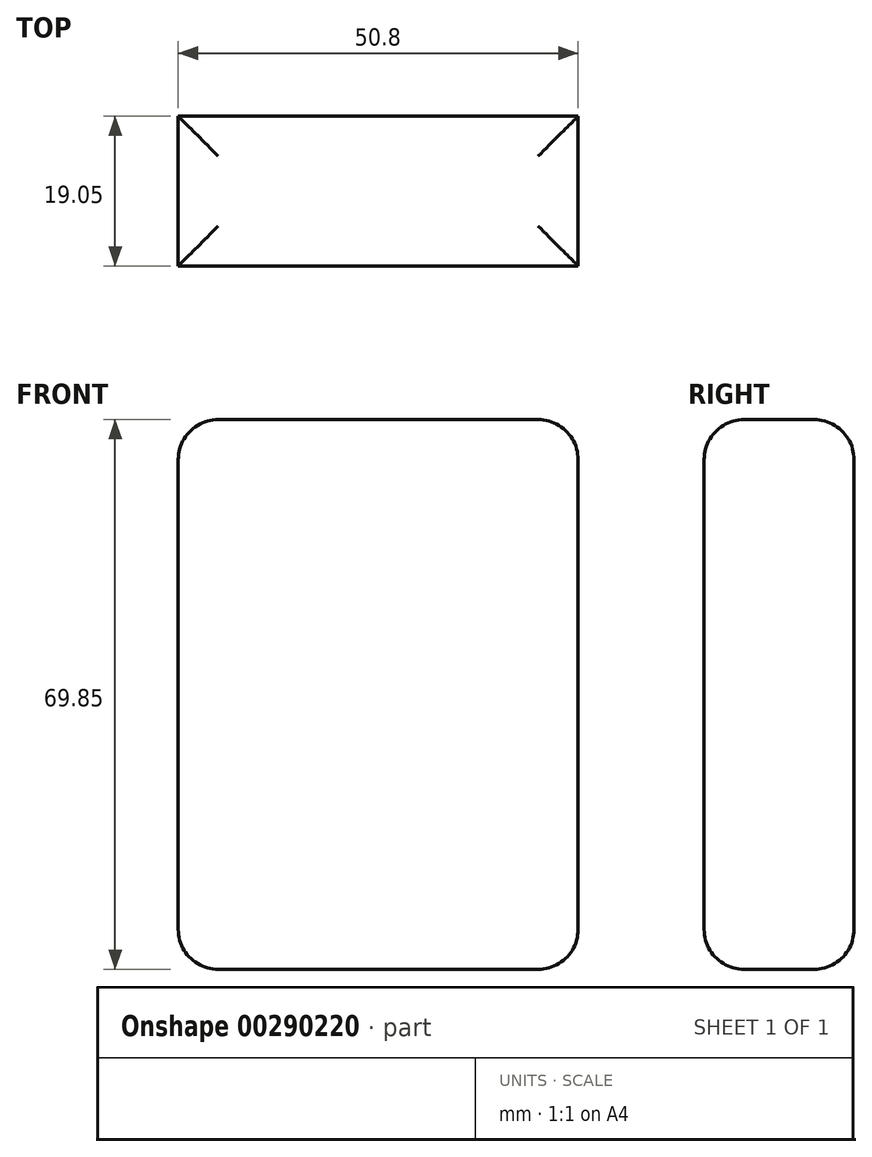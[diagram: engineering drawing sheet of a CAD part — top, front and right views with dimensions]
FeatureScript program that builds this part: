
annotation { "Feature Type Name" : "Feature", "Feature Type Description" : "" }
export const myFeature = defineFeature(function(context is Context, id is Id, definition is map)
    precondition{}
    {
        {
            var Q0;
            Q0=qCreatedBy(makeId("Front.planeOp"),FACE);
            var sketch = newSketch(context, id + "F0", { "sketchPlane" : qUnion([Q0])});
            skLineSegment(sketch, "E0.bottom", {"start": v(0, 0) * mm, "end": v(-50.8, 0) * mm});
            skLineSegment(sketch, "E0.top", {"start": v(0, 69.85) * mm, "end": v(-50.8, 69.85) * mm});
            skLineSegment(sketch, "E0.left", {"start": v(0, 0) * mm, "end": v(0, 69.85) * mm});
            skLineSegment(sketch, "E0.right", {"start": v(-50.8, 0) * mm, "end": v(-50.8, 69.85) * mm});
            skSolve(sketch);
        }
        {
            var Q0;
            Q0=makeQuery(id+"F0.imprint","IMPRINT",FACE,{"disambiguationData":[TD([[makeQuery(id+"F0.imprint","IMPRINT",EDGE,{"derivedFrom":sQuery(id+"F0.wireOp",EDGE,"E0.bottom")}),-1.0]])]});
            extrude(context, id + "F1", {"entities" : qUnion([Q0]), "depth" : 19.05 * mm});
        }
        {
            var Q0;
            Q0=makeQuery(id+"F1.opExtrude","SWEPT_FACE",FACE,{"disambiguationData":[OSD([sQuery(id+"F0.wireOp",EDGE,"E0.top")])]});
            fillet(context, id + "F2", {"entities" : qUnion([Q0]), "radius" : 5.08 * mm, "tangentPropagation" : true, "allowEdgeOverflow" : false});
        }
        {
            var Q0;
            Q0=makeQuery(id+"F1.opExtrude","SWEPT_FACE",FACE,{"disambiguationData":[OSD([sQuery(id+"F0.wireOp",EDGE,"E0.bottom")])]});
            fillet(context, id + "F3", {"entities" : qUnion([Q0]), "radius" : 5.08 * mm, "tangentPropagation" : true, "allowEdgeOverflow" : false});
        }
    });
